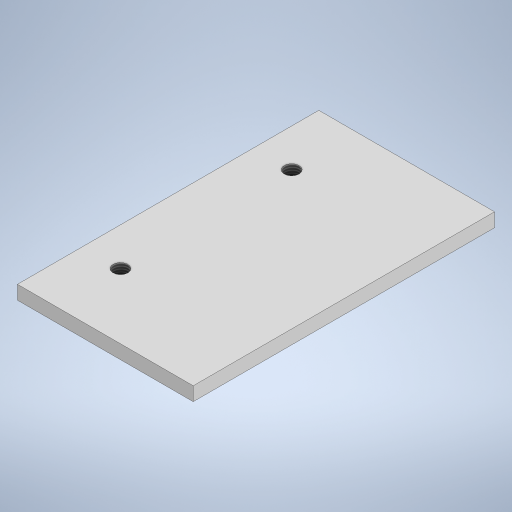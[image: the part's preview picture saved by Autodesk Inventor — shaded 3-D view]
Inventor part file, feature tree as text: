
AUTODESK INVENTOR PART (.ipt)
format: ipt  version: 2023 (Build 270158000, 158)  size: 217,088 bytes
history: native  units: mm
features: sketch x2, extrude x1, hole x1
ambient origin geometry x8: Origin, YZ Plane, XZ Plane, XY Plane, X Axis, Y Axis, Z Axis, Center Point
bodies: Solid1 (feature_tree)
feature tree (4):
  extrude  "Extrusion1"  Depth=70.0mm
  hole  "Hole1"  [1 undecoded]
  sketch  "Sketch1"  dims[d0=120.0mm d1=70.0mm]
  sketch  "Sketch2"  dims[d2=5.5mm d3=0.0mm d4=30.0mm d5=30.0mm d6=5.917468mm d7=14.0mm d8=4.0mm d9=2.0mm d10=90.0deg d11=19.1mm d12=20.594885mm]
note: 1 required parameter value undecoded (feature->parameter linkage not recoverable at this tier; creation-order binding heuristic only, values carry confidence <= 0.55)
